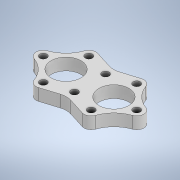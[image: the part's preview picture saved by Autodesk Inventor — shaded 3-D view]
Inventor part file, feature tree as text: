
AUTODESK INVENTOR PART (.ipt)
format: ipt  version: 2021 (Build 250183000, 183)  size: 173,056 bytes
history: native  units: mm
features: extrude x1, sketch x1
ambient origin geometry x8: Origin, YZ Plane, XZ Plane, XY Plane, X Axis, Y Axis, Z Axis, Center Point
bodies: Solid1 (feature_tree)
feature tree (2):
  extrude  "Extrusion1"  Depth=10.0mm
  sketch  "Sketch1"  dims[d26=38.0mm d27=12.566371mm d28=12.566371mm d29=12.566371mm d30=12.566371mm d46=25.0mm d47=38.0mm d48=12.0mm d49=12.0mm d50=12.0mm d51=50.0mm d52=26.870058mm d53=26.870058mm d54=50.0mm d55=20.0mm d56=6.0mm d57=6.0mm d58=13.0mm d59=13.0mm d60=6.0mm d61=6.0mm d62=6.0mm d65=19.0mm d66=19.0mm d67=19.0mm d68=6.0mm d69=6.0mm d70=2.0mm d71=15.0mm d72=10.0mm d73=0.0mm]
